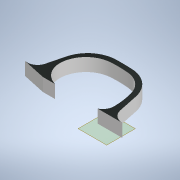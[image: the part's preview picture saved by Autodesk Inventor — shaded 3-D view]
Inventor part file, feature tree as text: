
AUTODESK INVENTOR PART (.ipt)
format: ipt  version: 2022 (Build 260153000, 153)  size: 4,166,656 bytes
history: native  units: mm
features: other x2, extrude x1, sketch x1
ambient origin geometry x8: Origin, YZ Plane, XZ Plane, XY Plane, X Axis, Y Axis, Z Axis, Center Point
bodies: Body1 (feature_tree)
feature tree (4):
  other  "РабПлоскость1"
  extrude  "Выдавливание1"  Depth=10.0mm TaperAngle=0.0deg
  sketch  "Эскиз1"
  other  "Картинка1"
